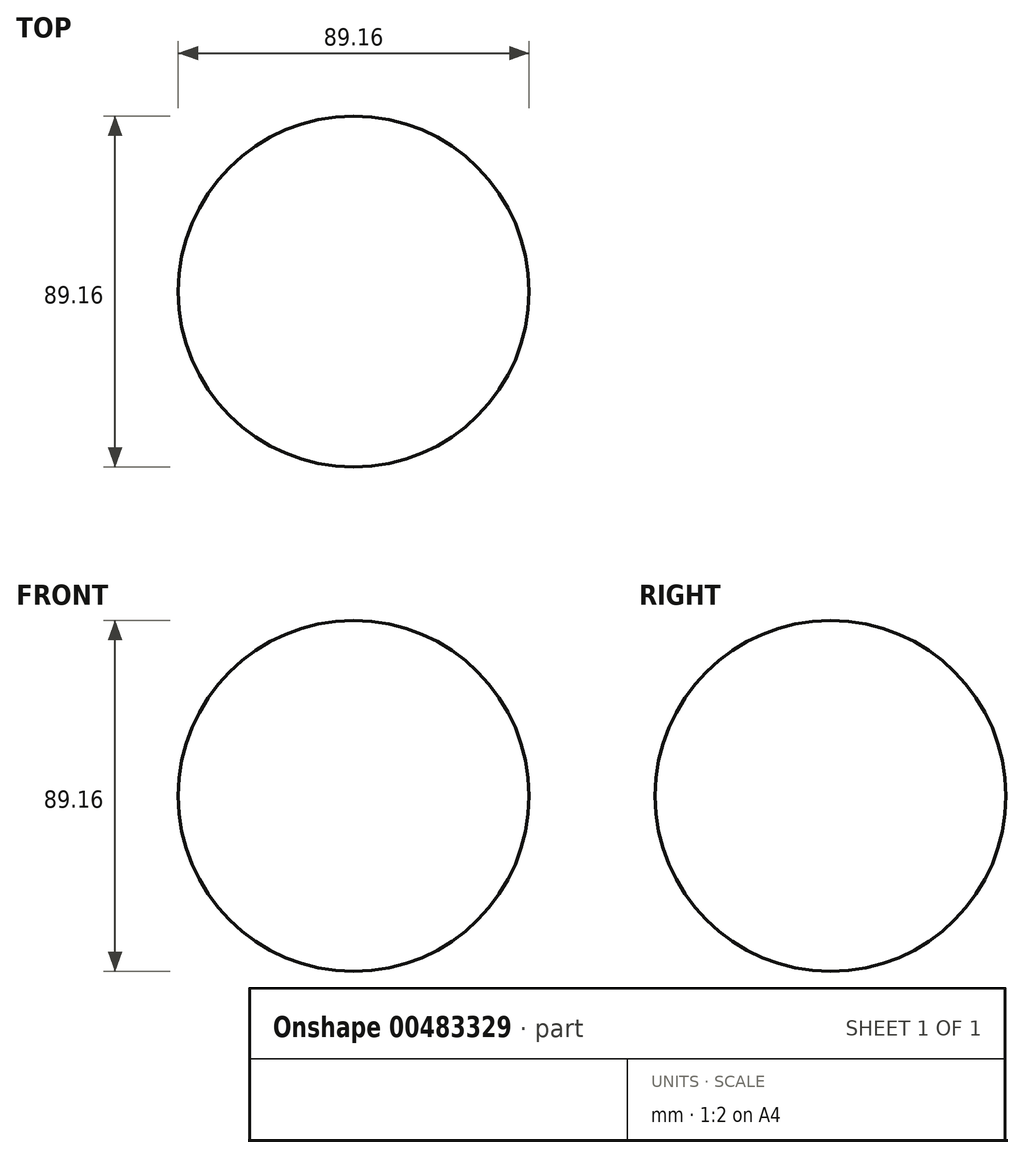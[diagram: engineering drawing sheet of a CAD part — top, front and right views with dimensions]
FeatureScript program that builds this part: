
annotation { "Feature Type Name" : "Feature", "Feature Type Description" : "" }
export const myFeature = defineFeature(function(context is Context, id is Id, definition is map)
    precondition{}
    {
        {
            var Q0;
            Q0=qCreatedBy(makeId("Top.planeOp"),FACE);
            var sketch = newSketch(context, id + "F0", { "sketchPlane" : qUnion([Q0])});
            skArc(sketch, "E0", {"start": v(0, 44.58) * mm, "mid": v(-44.58, 0) * mm, "end": v(0, -44.58) * mm});
            skLineSegment(sketch, "E1", {"start": v(0, -44.58) * mm, "end": v(0, 44.58) * mm});
            skSolve(sketch);
        }
        {
            var Q0;
            Q0=makeQuery(id+"F0.imprint","IMPRINT",FACE,{"disambiguationData":[TD([[makeQuery(id+"F0.imprint","IMPRINT",EDGE,{"derivedFrom":sQuery(id+"F0.wireOp",EDGE,"E0")}),1.0]])]});
            var Q1;
            Q1=sQuery(id+"F0.wireOp",EDGE,"E1");
            revolve(context, id + "F1", {"entities" : qUnion([Q0]), "axis" : qUnion([Q1]), "revolveType" : RevolveType.FULL});
        }
    });
